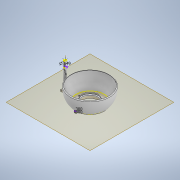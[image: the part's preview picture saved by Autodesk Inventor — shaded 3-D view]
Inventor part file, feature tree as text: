
AUTODESK INVENTOR PART (.ipt)
format: ipt  version: 2020 (Build 240168000, 168)  size: 537,088 bytes
history: native  units: in
note: dims shown in document units (in); Inventor stores cm internally (conversion verified against a paired STEP export)
features: sketch x10, extrude x5, hole x3, fillet x3, other x3, revolve x1, plane x1, mirror x1, helix x1
ambient origin geometry x8: Origin, YZ Plane, XZ Plane, XY Plane, X Axis, Y Axis, Z Axis, Center Point
bodies: Solid1 (feature_tree)
feature tree (28):
  revolve  "Revolution1"  [1 undecoded]
  plane  "Work Plane1"
  sketch  "Sketch2"  dims[d2=0.125in d3=3.0in]
  extrude  "Extrusion1"  Depth=3.0in
  hole  "Hole1"  [1 undecoded]
  hole  "Hole4"  [1 undecoded]
  hole  "Hole5"  [1 undecoded]
  fillet  "Fillet1"  Radius=0.85in
  mirror  "Mirror1"
  fillet  "Fillet2"  Radius=3.0in
  fillet  "Fillet3"  Radius=0.125in
  extrude  "Extrusion2"  TaperAngle=90.0deg  [1 undecoded]
  extrude  "Extrusion3"  Depth=0.75in
  extrude  "Extrusion4"  Depth=0.35in TaperAngle=0.0deg
  sketch  "3D Sketch1"
  other  "Work Axis1"
  helix  "Coil1"  [1 undecoded]
  extrude  "Extrusion5"  Depth=0.5in
  sketch  "Sketch1"  dims[d0=1.26in d1=0.0in]
  other  "Work Point1"
  sketch  "Sketch4"  dims[d4=3.0in d5=1.0in]
  sketch  "Sketch5"  dims[d6=0.125in d7=1.0in]
  sketch  "Sketch6"  dims[d8=0.5in d9=0.125in d10=0.85in d11=3.0in d12=0.125in]
  sketch  "Sketch7"  dims[d13=3.0in d14=90.0deg]
  sketch  "Sketch8"  dims[d15=0.125in d16=0.75in d17=0.125in d18=0.25in d19=0.5635in d20=0.25in d21=0.0in d22=0.3in]
  other  "Helical Curve2"
  sketch  "Sketch9"  dims[d23=0.3in d24=0.35in d25=0.0in d41=1.75in]
  sketch  "Sketch10"  dims[d42=0.266in d43=0.75in d44=0.438in d45=0.25in d46=0.5635in d47=6.0in d48=0.0in d49=0.15in d50=0.125in d51=0.75in d52=0.438in d53=0.25in d54=0.5635in d55=0.2in d56=0.0in d57=0.0625in d58=0.125in d59=0.0625in d60=0.25in d61=90.0deg d62=0.5in d63=3.0in d64=0.25in d65=3.0in d66=0.25in d67=0.5in d68=0.5in d69=0.0in d70=0.375in d71=4.0in d72=0.0in d73=0.0625in d74=0.125in d75=0.025in d76=1.0in d77=0.0in d83=2.0in d84=0.0984in d85=0.549in d86=0.0in d87=0.125in d88=1.0in d89=1.0in d90=0.0984in d91=0.0in d92=90.0deg d93=90.0deg d94=45.0deg d95=0.0in d96=0.275in d97=0.0in]
note: 6 required parameter values undecoded (feature->parameter linkage not recoverable at this tier; creation-order binding heuristic only, values carry confidence <= 0.55)